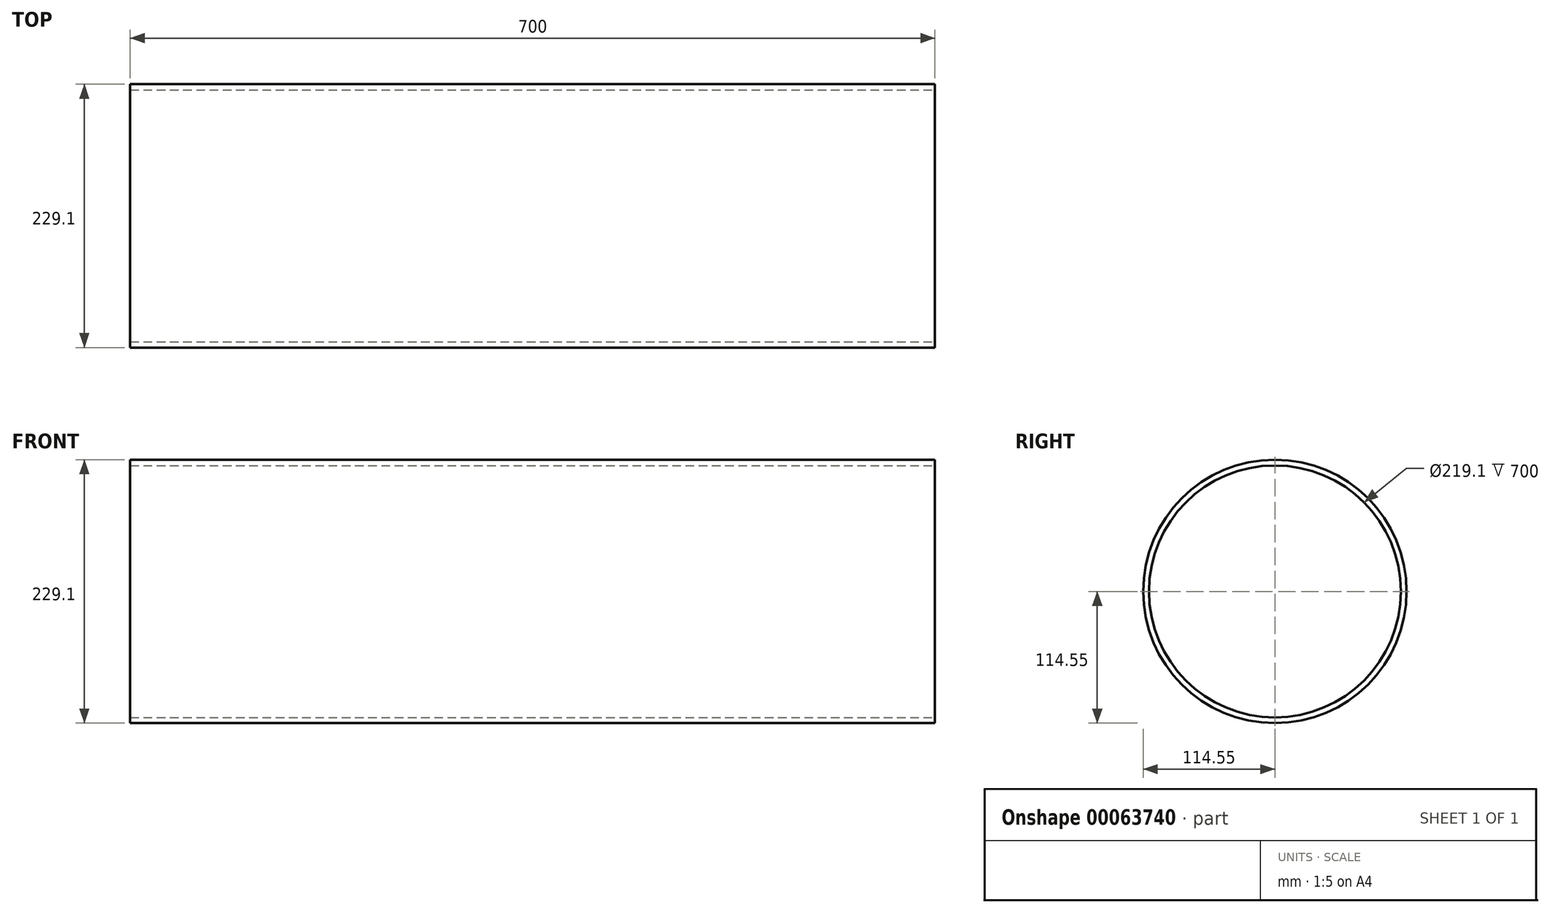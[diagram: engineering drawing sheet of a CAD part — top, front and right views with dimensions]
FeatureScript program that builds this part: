
annotation { "Feature Type Name" : "Feature", "Feature Type Description" : "" }
export const myFeature = defineFeature(function(context is Context, id is Id, definition is map)
    precondition{}
    {
        {
            var Q0;
            Q0=qCreatedBy(makeId("Right.planeOp"),FACE);
            var sketch = newSketch(context, id + "F0", { "sketchPlane" : qUnion([Q0])});
            skCircle(sketch, "E0", {"center": v(0, 0) * mm, "radius": 109.55 * mm});
            skCircle(sketch, "E1", {"center": v(0, 0) * mm, "radius": 114.55 * mm});
            skSolve(sketch);
        }
        {
            var Q0;
            Q0=makeQuery(id+"F0.imprint","IMPRINT",FACE,{"disambiguationData":[TD([[makeQuery(id+"F0.imprint","IMPRINT",EDGE,{"derivedFrom":sQuery(id+"F0.wireOp",EDGE,"E0")}),-1.0]])]});
            extrude(context, id + "F1", {"entities" : qUnion([Q0]), "oppositeDirection" : true, "depth" : 700 * mm});
        }
    });
